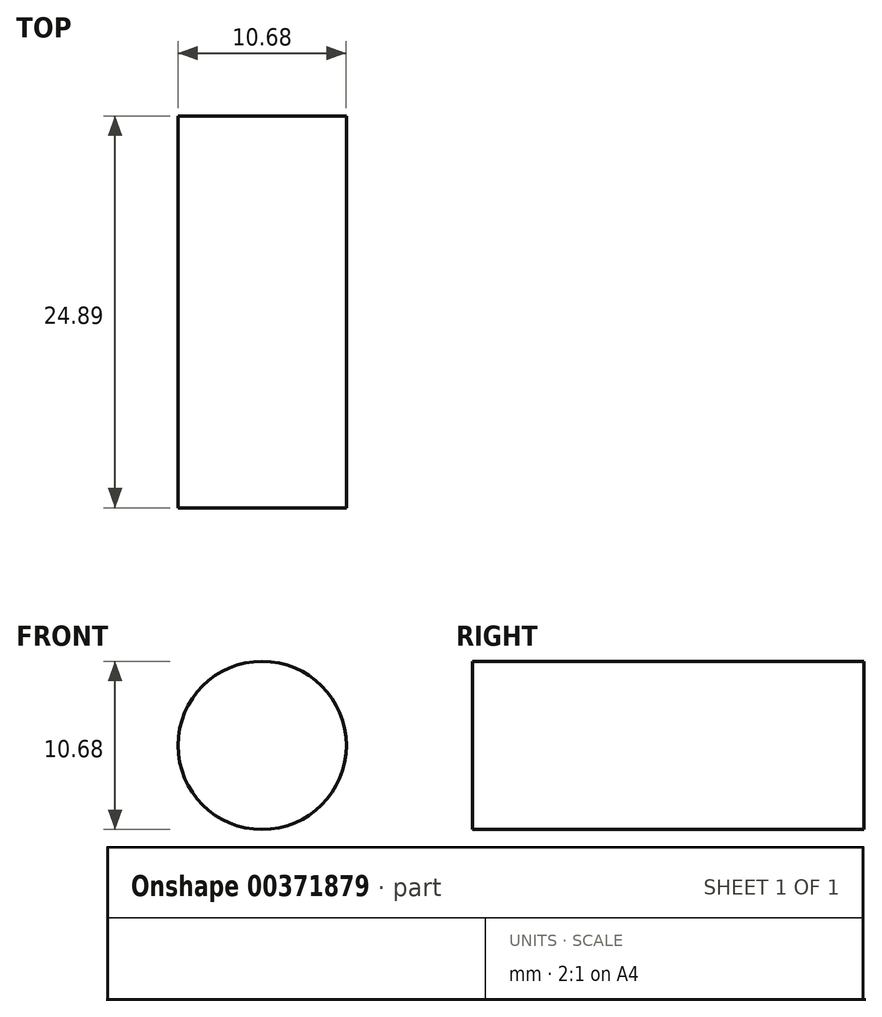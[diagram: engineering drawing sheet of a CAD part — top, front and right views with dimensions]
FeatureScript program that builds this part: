
annotation { "Feature Type Name" : "Feature", "Feature Type Description" : "" }
export const myFeature = defineFeature(function(context is Context, id is Id, definition is map)
    precondition{}
    {
        {
            var Q0;
            Q0=qCreatedBy(makeId("Top.planeOp"),FACE);
            var sketch = newSketch(context, id + "F0", { "sketchPlane" : qUnion([Q0])});
            skLineSegment(sketch, "E0.bottom", {"start": v(0, 0) * mm, "end": v(5.34, 0) * mm});
            skLineSegment(sketch, "E0.top", {"start": v(0, -24.89) * mm, "end": v(5.34, -24.89) * mm});
            skLineSegment(sketch, "E0.left", {"start": v(0, 0) * mm, "end": v(0, -24.89) * mm});
            skLineSegment(sketch, "E0.right", {"start": v(5.34, 0) * mm, "end": v(5.34, -24.89) * mm});
            skSolve(sketch);
        }
        {
            var Q0;
            Q0 = qSketchRegion(id + "F0", true);
            var Q1;
            Q1=sQuery(id+"F0.wireOp",EDGE,"E0.left");
            revolve(context, id + "F1", {"surfaceOperationType" : NewSurfaceOperationType.NEW, "entities" : qUnion([Q0]), "axis" : qUnion([Q1]), "revolveType" : RevolveType.FULL});
        }
    });
